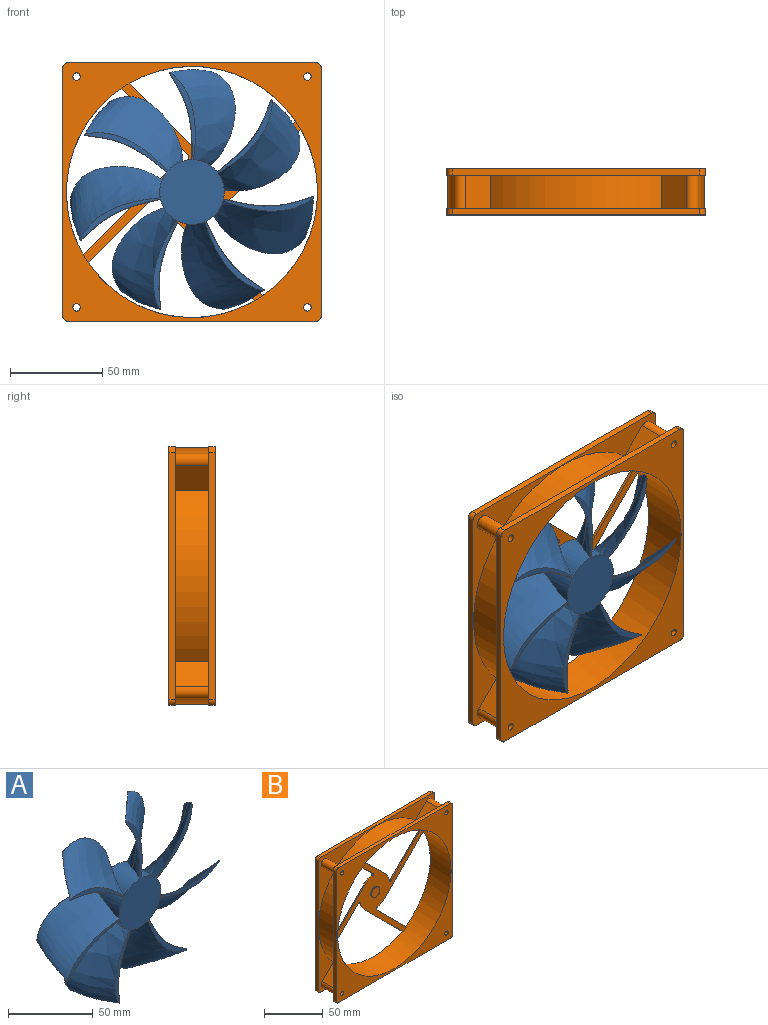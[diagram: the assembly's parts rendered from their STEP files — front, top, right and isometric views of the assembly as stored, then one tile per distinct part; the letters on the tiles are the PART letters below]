
ASSEMBLY  parts=2 mates=1
PART A: 53 faces, bbox 133.5x21x131.3 mm
  f0: cylinder r=17.5mm len=22.57mm, axis (0,1,0), area 289.4mm2, adj f7,f8,f39,f40,f41,f42,f43,f44
  f1: cylinder r=17.5mm len=20mm, axis (0,1,0), area 289.4mm2, adj f7,f8,f33,f34,f35,f36,f37,f38
  f2: cylinder r=17.5mm len=21.63mm, axis (0,1,0), area 289.4mm2, adj f7,f8,f27,f28,f29,f30,f31,f32
  f3: cylinder r=17.5mm len=21.05mm, axis (0,1,0), area 289.4mm2, adj f7,f8,f21,f22,f23,f24,f25,f26
  f4: cylinder r=17.5mm len=20mm, axis (0,1,0), area 289.4mm2, adj f7,f8,f15,f16,f17,f18,f19,f20
  f5: cylinder r=17.5mm len=22.37mm, axis (0,1,0), area 289.4mm2, adj f7,f8,f9,f10,f11,f12,f13,f14
  f6: cylinder r=17.5mm len=20mm, axis (0,1,0), area 289.4mm2, adj f7,f8,f11,f12,f45,f46,f47,f48
  f7: plane 128.51x126.49mm, normal (0,-1,0), area 1774.1mm2, adj f0,f1,f2,f3,f4,f5,f6,f10
  f8: plane 130.09x129.27mm, normal (0,1,0), area 1953.1mm2, adj f0,f1,f2,f3,f4,f5,f6,f12
  f9: extruded ~49.4x8.67mm, area 5.2mm2, adj f5,f11,f14
  f10: extruded ~47.32x12.17mm, area 5mm2, adj f5,f7,f11,f13
  f11: bspline ~53.42x35.53mm, area 2950.8mm2, adj f5,f6,f7,f9,f10,f12,f13,f14
  f12: extruded ~50.81x14.23mm, area 11.7mm2, adj f5,f6,f8,f11
  f13: plane 48.68x13.49mm, normal (0,1,0), area 4.2mm2, adj f5,f10,f11
  f14: plane 50.87x10.03mm, normal (0,1,0), area 5mm2, adj f5,f9,f11
  f15: extruded ~41.56x27.3mm, area 5.2mm2, adj f4,f17,f20
  f16: extruded ~44.45x20.21mm, area 5mm2, adj f4,f7,f17,f19
  f17: bspline ~53.38x42.98mm, area 2950.8mm2, adj f4,f5,f7,f15,f16,f18,f19,f20
  f18: extruded ~39.74x35.17mm, area 11.7mm2, adj f4,f5,f8,f17
  f19: plane 45.83x21.57mm, normal (0,1,0), area 4.2mm2, adj f4,f16,f17
  f20: plane 43.03x28.77mm, normal (0,1,0), area 5mm2, adj f4,f15,f17
  f21: extruded ~47.17x16.17mm, area 5.2mm2, adj f3,f23,f26
  f22: extruded ~43.49x22.27mm, area 5mm2, adj f3,f7,f23,f25
  f23: bspline ~53.43x40.1mm, area 2950.8mm2, adj f3,f4,f7,f21,f22,f24,f25,f26
  f24: extruded ~49.57x18.53mm, area 11.7mm2, adj f3,f4,f8,f23
  f25: plane 44.85x23.6mm, normal (0,1,0), area 4.2mm2, adj f3,f22,f23
  f26: plane 48.63x17.61mm, normal (0,1,0), area 5mm2, adj f3,f21,f23
  f27: extruded ~46.52x17.4mm, area 5.2mm2, adj f2,f29,f32
  f28: extruded ~47.79x10.32mm, area 5mm2, adj f2,f7,f29,f31
  f29: bspline ~56x37.26mm, area 2950.8mm2, adj f2,f3,f7,f27,f28,f30,f31,f32
  f30: extruded ~45.79x28.45mm, area 11.7mm2, adj f2,f3,f8,f29
  f31: plane 49.19x11.68mm, normal (0,1,0), area 4.2mm2, adj f2,f28,f29
  f32: plane 48x18.87mm, normal (0,1,0), area 5mm2, adj f2,f27,f29
  f33: extruded ~42.57x25.73mm, area 5.2mm2, adj f1,f35,f38
  f34: extruded ~37.48x31.36mm, area 5mm2, adj f1,f7,f35,f37
  f35: bspline ~50.84x44.77mm, area 2950.8mm2, adj f1,f2,f7,f33,f34,f36,f37,f38
  f36: extruded ~46.1x24.93mm, area 11.7mm2, adj f1,f2,f8,f35
  f37: plane 38.84x32.71mm, normal (0,1,0), area 4.2mm2, adj f1,f34,f35
  f38: plane 44.03x27.21mm, normal (0,1,0), area 5mm2, adj f1,f33,f35
  f39: extruded ~49.16x9.74mm, area 5.2mm2, adj f0,f41,f44
  f40: extruded ~48.78x4.98mm, area 5mm2, adj f0,f7,f41,f43
  f41: bspline ~55.23x30.98mm, area 2950.8mm2, adj f0,f1,f7,f39,f40,f42,f43,f44
  f42: extruded ~49.54x21.2mm, area 11.7mm2, adj f0,f1,f8,f41
  f43: plane 50.16x6.3mm, normal (0,1,0), area 4.2mm2, adj f0,f40,f41
  f44: plane 50.66x11.18mm, normal (0,1,0), area 5mm2, adj f0,f39,f41
  f45: extruded ~35.83x34.51mm, area 5.2mm2, adj f6,f47,f50
  f46: extruded ~38.88x29.59mm, area 5mm2, adj f6,f7,f47,f49
  f47: bspline ~49.33x47.53mm, area 2950.8mm2, adj f0,f6,f7,f45,f46,f48,f49,f50
  f48: extruded ~41.09x32.19mm, area 11.7mm2, adj f0,f6,f8,f47
  f49: plane 40.25x30.95mm, normal (0,1,0), area 4.2mm2, adj f6,f46,f47
  f50: plane 37.3x35.98mm, normal (0,1,0), area 5mm2, adj f6,f45,f47
  f51: cylinder r=5mm len=10mm, axis (0,-1,0), area 31.4mm2, adj f8,f52
  f52: plane 10x10mm, normal (0,1,0), area 78.5mm2, adj f51
PART B: 60 faces, bbox 140x25x140 mm
  f0: cylinder r=3mm len=3.5mm, axis (0,1,0), area 16.5mm2, adj f1,f7,f22,f40
  f1: plane 134x3.5mm, normal (0,0,1), area 469mm2, adj f0,f2,f22,f40
  f2: cylinder r=3mm len=3.5mm, axis (0,1,0), area 16.5mm2, adj f1,f3,f22,f40
  f3: plane 134x3.5mm, normal (-1,0,0), area 469mm2, adj f2,f4,f22,f40
  f4: cylinder r=3mm len=3.5mm, axis (0,1,0), area 16.5mm2, adj f3,f5,f22,f40
  f5: plane 134x3.5mm, normal (0,0,-1), area 469mm2, adj f4,f6,f22,f40
  f6: cylinder r=3mm len=3.5mm, axis (0,1,0), area 16.5mm2, adj f5,f7,f22,f40
  f7: plane 134x3.5mm, normal (1,0,0), area 469mm2, adj f0,f6,f22,f40
  f8: cylinder r=3mm len=3.5mm, axis (0,1,0), area 16.5mm2, adj f9,f20,f21,f41
  f9: plane 134x3.5mm, normal (0,0,1), area 469mm2, adj f8,f10,f21,f41
  f10: cylinder r=3mm len=3.5mm, axis (0,1,0), area 16.5mm2, adj f9,f11,f21,f41
  f11: plane 134x3.5mm, normal (-1,0,0), area 469mm2, adj f10,f12,f21,f41
  f12: cylinder r=3mm len=3.5mm, axis (0,1,0), area 16.5mm2, adj f11,f13,f21,f41
  f13: plane 134x3.5mm, normal (0,0,-1), area 469mm2, adj f12,f14,f21,f41
  f14: cylinder r=3mm len=3.5mm, axis (0,1,0), area 16.5mm2, adj f13,f20,f21,f41
  f15: cylinder r=68mm len=136mm, axis (0,1,0), area 10650.6mm2, adj f21,f22,f23,f26,f27,f30,f31,f34
  f16: cylinder r=2mm len=25mm, axis (0,1,0), area 314.2mm2, adj f21,f22
  f17: cylinder r=2mm len=25mm, axis (0,1,0), area 314.2mm2, adj f21,f22
  f18: cylinder r=2mm len=25mm, axis (0,1,0), area 314.2mm2, adj f21,f22
  f19: cylinder r=2mm len=25mm, axis (0,1,0), area 314.2mm2, adj f21,f22
  f20: plane 134x3.5mm, normal (1,0,0), area 469mm2, adj f8,f14,f21,f41
  f21: plane 140x140mm, normal (0,-1,0), area 5015.3mm2, adj f8,f9,f10,f11,f12,f13,f14,f15
  f22: plane 140x140mm, normal (0,1,0), area 7143.6mm2, adj f0,f1,f2,f3,f4,f5,f6,f7
  f23: plane 46.46x46.46mm, normal (0.71,0,-0.71), area 98.6mm2, adj f15,f22,f24,f39
  f24: cylinder r=17.5mm len=9.45mm, axis (0,1,0), area 16.2mm2, adj f22,f23,f25,f39
  f25: cylinder r=1.5mm len=2.54mm, axis (0,1,0), area 4.9mm2, adj f22,f24,f26,f39
  f26: plane 36.31x36.31mm, normal (0.71,0,0.71), area 77mm2, adj f15,f22,f25,f39
  f27: plane 46.46x46.46mm, normal (-0.71,0,-0.71), area 98.6mm2, adj f15,f22,f28,f39
  f28: cylinder r=17.5mm len=9.45mm, axis (0,1,0), area 16.2mm2, adj f22,f27,f29,f39
  f29: cylinder r=1.5mm len=2.54mm, axis (0,1,0), area 4.9mm2, adj f22,f28,f30,f39
  f30: plane 36.31x36.31mm, normal (0.71,0,-0.71), area 77mm2, adj f15,f22,f29,f39
  f31: plane 46.46x46.46mm, normal (-0.71,0,0.71), area 98.6mm2, adj f15,f22,f32,f39
  f32: cylinder r=17.5mm len=9.45mm, axis (0,1,0), area 16.2mm2, adj f22,f31,f33,f39
  f33: cylinder r=1.5mm len=2.54mm, axis (0,1,0), area 4.9mm2, adj f22,f32,f34,f39
  f34: plane 36.31x36.31mm, normal (-0.71,0,-0.71), area 77mm2, adj f15,f22,f33,f39
  f35: plane 46.46x46.46mm, normal (0.71,0,0.71), area 98.6mm2, adj f15,f22,f36,f39
  f36: cylinder r=17.5mm len=9.45mm, axis (0,1,0), area 16.2mm2, adj f22,f35,f37,f39
  f37: cylinder r=1.5mm len=2.54mm, axis (0,1,0), area 4.9mm2, adj f22,f36,f38,f39
  f38: plane 36.31x36.31mm, normal (-0.71,0,0.71), area 77mm2, adj f15,f22,f37,f39
  f39: plane 117.68x117.68mm, normal (0,-1,0), area 2049.7mm2, adj f15,f23,f24,f25,f26,f27,f28,f29
  f40: plane 140x140mm, normal (0,-1,0), area 3711.4mm2, adj f0,f1,f2,f3,f4,f5,f6,f7
  f41: plane 140x140mm, normal (0,1,0), area 3711.4mm2, adj f8,f9,f10,f11,f12,f13,f14,f20
  f42: plane 18x13.44mm, normal (-0.71,0,0.71), area 342.1mm2, adj f40,f41,f43,f57
  f43: cylinder r=4mm len=18mm, axis (0,-1,0), area 226.2mm2, adj f40,f41,f42,f44
  f44: plane 18x13.44mm, normal (0.71,0,-0.71), area 342.1mm2, adj f40,f41,f43,f45
  f45: cylinder r=69.5mm len=92.47mm, axis (0,-1,0), area 1821mm2, adj f40,f41,f44,f46
  f46: plane 18x13.44mm, normal (0.71,0,0.71), area 342.1mm2, adj f40,f41,f45,f47
  f47: cylinder r=4mm len=18mm, axis (0,-1,0), area 226.2mm2, adj f40,f41,f46,f48
  f48: plane 18x13.44mm, normal (-0.71,0,-0.71), area 342.1mm2, adj f40,f41,f47,f49
  f49: cylinder r=69.5mm len=92.47mm, axis (0,-1,0), area 1821mm2, adj f40,f41,f48,f50
  f50: plane 18x13.44mm, normal (0.71,0,-0.71), area 342.1mm2, adj f40,f41,f49,f51
  f51: cylinder r=4mm len=18mm, axis (0,-1,0), area 226.2mm2, adj f40,f41,f50,f52
  f52: plane 18x13.44mm, normal (-0.71,0,0.71), area 342.1mm2, adj f40,f41,f51,f53
  f53: cylinder r=69.5mm len=92.47mm, axis (0,-1,0), area 1821mm2, adj f40,f41,f52,f54
  f54: plane 18x13.44mm, normal (-0.71,0,-0.71), area 342.1mm2, adj f40,f41,f53,f55
  f55: cylinder r=4mm len=18mm, axis (0,-1,0), area 226.2mm2, adj f40,f41,f54,f56
  f56: plane 18x13.44mm, normal (0.71,0,0.71), area 342.1mm2, adj f40,f41,f55,f57
  f57: cylinder r=69.5mm len=92.47mm, axis (0,-1,0), area 1821mm2, adj f40,f41,f42,f56
  f58: cylinder r=5mm len=10mm, axis (0,1,0), area 31.4mm2, adj f39,f59
  f59: plane 10x10mm, normal (0,-1,0), area 78.5mm2, adj f58
PLACE A t=(0,-12.5,0)mm
PLACE B t=(0,-12.5,0)mm
MATE revolute A.f0 <-> B.f15  axis (0,1,0) through (0,-2.5,0)mm
